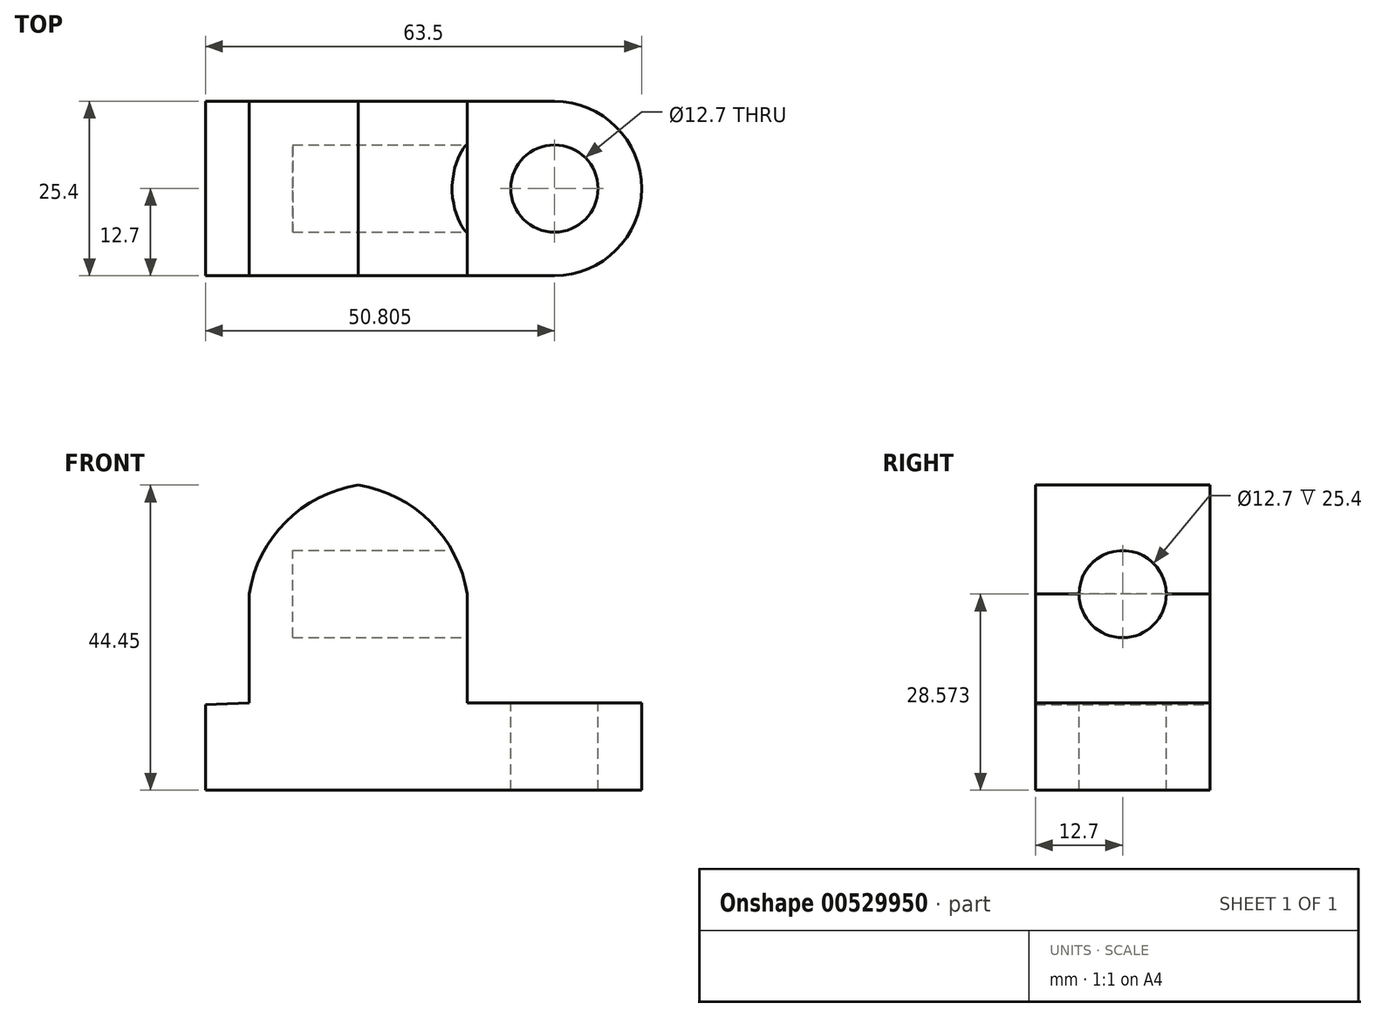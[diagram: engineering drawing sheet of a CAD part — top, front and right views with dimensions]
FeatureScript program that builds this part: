
annotation { "Feature Type Name" : "Feature", "Feature Type Description" : "" }
export const myFeature = defineFeature(function(context is Context, id is Id, definition is map)
    precondition{}
    {
        {
            var Q0;
            Q0=qCreatedBy(makeId("Front.planeOp"),FACE);
            var sketch = newSketch(context, id + "F0", { "sketchPlane" : qUnion([Q0])});
            skLineSegment(sketch, "E0", {"start": v(-67.73, 16.19) * mm, "end": v(-4.23, 16.19) * mm});
            skLineSegment(sketch, "E1", {"start": v(-4.23, 16.19) * mm, "end": v(-4.23, 28.89) * mm});
            skLineSegment(sketch, "E2", {"start": v(-4.23, 28.89) * mm, "end": v(-29.63, 28.89) * mm});
            skLineSegment(sketch, "E3", {"start": v(-29.63, 28.89) * mm, "end": v(-29.63, 60.64) * mm});
            skLineSegment(sketch, "E4", {"start": v(-29.63, 60.64) * mm, "end": v(-61.38, 60.64) * mm});
            skLineSegment(sketch, "E5", {"start": v(-61.38, 60.64) * mm, "end": v(-61.38, 28.89) * mm});
            skLineSegment(sketch, "E6", {"start": v(-67.73, 16.19) * mm, "end": v(-67.73, 28.64) * mm});
            skLineSegment(sketch, "E7", {"start": v(-67.73, 28.64) * mm, "end": v(-61.38, 28.89) * mm});
            skSolve(sketch);
        }
        {
            var Q0;
            Q0 = qSketchRegion(id + "F0", true);
            var Q1;
            Q1=makeQuery(id+"F0.imprint","IMPRINT",FACE,{"disambiguationData":[TD([[makeQuery(id+"F0.imprint","IMPRINT",EDGE,{"derivedFrom":sQuery(id+"F0.wireOp",EDGE,"E0")}),1.0]])]});
            extrude(context, id + "F1", {"entities" : qUnion([Q0, Q1]), "depth" : 25.4 * mm, "offsetDistance" : 25.4 * mm});
        }
        {
            var Q0;
            Q0=makeQuery(id+"F1.opExtrude","SWEPT_FACE",FACE,{"disambiguationData":[OSD([sQuery(id+"F0.wireOp",EDGE,"E2")])]});
            var sketch = newSketch(context, id + "F2", { "sketchPlane" : qUnion([Q0])});
            skArc(sketch, "E8", {"start": v(-16.93, -25.4) * mm, "mid": v(-4.23, -12.7) * mm, "end": v(-16.93, 0) * mm});
            skSolve(sketch);
        }
        {
            var Q0;
            {var subQ0=sQuery(id+"F2.wireOp",EDGE,"E8");var subQ1=sQuery(id+"F0.wireOp",EDGE,"E2");var subQ4=makeQuery(id+"F1.opExtrude","CAP_EDGE",EDGE,{"disambiguationData":[OSD([subQ1])],"isStart":true});var subQ5=makeQuery(id+"F2.imprint","INTERSECT",VERTEX,{"derivedFrom":[subQ4,subQ0]});Q0=makeQuery(id+"F2.imprint","IMPRINT",FACE,{"disambiguationData":[TD([[makeQuery(id+"F2.imprint","IMPRINT",EDGE,{"disambiguationData":[TD([[subQ5,1.0]])],"derivedFrom":subQ0}),-1.0]])]});}
            var Q1;
            {var subQ0=sQuery(id+"F2.wireOp",EDGE,"E8");var subQ1=sQuery(id+"F0.wireOp",EDGE,"E2");var subQ4=makeQuery(id+"F1.opExtrude","CAP_EDGE",EDGE,{"disambiguationData":[OSD([subQ1])],"isStart":false});var subQ5=makeQuery(id+"F2.imprint","INTERSECT",VERTEX,{"derivedFrom":[subQ4,subQ0]});Q1=makeQuery(id+"F2.imprint","IMPRINT",FACE,{"disambiguationData":[TD([[makeQuery(id+"F2.imprint","IMPRINT",EDGE,{"disambiguationData":[TD([[subQ5,-1.0]])],"derivedFrom":subQ0}),-1.0]])]});}
            extrude(context, id + "F3", {"entities" : qUnion([Q0, Q1]), "operationType" : NewBodyOperationType.REMOVE, "oppositeDirection" : true, "depth" : 25.4 * mm, "offsetDistance" : 25.4 * mm});
        }
        {
            var Q0;
            Q0=makeQuery(id+"F1.opExtrude","SWEPT_FACE",FACE,{"disambiguationData":[OSD([sQuery(id+"F0.wireOp",EDGE,"E2")])]});
            var sketch = newSketch(context, id + "F4", { "sketchPlane" : qUnion([Q0])});
            skCircle(sketch, "E9", {"center": v(-16.93, -12.7) * mm, "radius": 6.35 * mm});
            skSolve(sketch);
        }
        {
            var Q0;
            Q0=makeQuery(id+"F4.imprint","IMPRINT",FACE,{"disambiguationData":[TD([[makeQuery(id+"F4.imprint","IMPRINT",EDGE,{"derivedFrom":sQuery(id+"F4.wireOp",EDGE,"E9")}),1.0]])]});
            extrude(context, id + "F5", {"entities" : qUnion([Q0]), "operationType" : NewBodyOperationType.REMOVE, "oppositeDirection" : true, "depth" : 25.4 * mm, "offsetDistance" : 25.4 * mm});
        }
        {
            var Q0;
            Q0=makeQuery(id+"F1.opExtrude","CAP_FACE",FACE,{"disambiguationData":[OSD([sQuery(id+"F0.wireOp",EDGE,"E0"),sQuery(id+"F0.wireOp",EDGE,"E1"),sQuery(id+"F0.wireOp",EDGE,"E2"),sQuery(id+"F0.wireOp",EDGE,"E3"),sQuery(id+"F0.wireOp",EDGE,"E4"),sQuery(id+"F0.wireOp",EDGE,"E5"),sQuery(id+"F0.wireOp",EDGE,"E6"),sQuery(id+"F0.wireOp",EDGE,"E7")])],"isStart":false});
            var sketch = newSketch(context, id + "F6", { "sketchPlane" : qUnion([Q0])});
            skArc(sketch, "E10", {"start": v(-29.63, 44.76) * mm, "mid": v(-34.98, 55.29) * mm, "end": v(-45.5, 60.64) * mm});
            skArc(sketch, "E11", {"start": v(-45.5, 60.64) * mm, "mid": v(-56.02, 55.29) * mm, "end": v(-61.38, 44.76) * mm});
            skSolve(sketch);
        }
        {
            var Q0;
            {var subQ0=sQuery(id+"F6.wireOp",EDGE,"E10");Q0=makeQuery(id+"F6.imprint","IMPRINT",FACE,{"disambiguationData":[TD([[makeQuery(id+"F6.imprint","IMPRINT",EDGE,{"derivedFrom":subQ0}),-1.0]])]});}
            var Q1;
            {var subQ0=sQuery(id+"F6.wireOp",EDGE,"E11");Q1=makeQuery(id+"F6.imprint","IMPRINT",FACE,{"disambiguationData":[TD([[makeQuery(id+"F6.imprint","IMPRINT",EDGE,{"derivedFrom":subQ0}),-1.0]])]});}
            extrude(context, id + "F7", {"entities" : qUnion([Q0, Q1]), "operationType" : NewBodyOperationType.REMOVE, "oppositeDirection" : true, "depth" : 25.4 * mm, "offsetDistance" : 25.4 * mm});
        }
        {
            var Q0;
            Q0=makeQuery(id+"F1.opExtrude","SWEPT_FACE",FACE,{"disambiguationData":[OSD([sQuery(id+"F0.wireOp",EDGE,"E3")])]});
            var sketch = newSketch(context, id + "F8", { "sketchPlane" : qUnion([Q0])});
            skCircle(sketch, "E12", {"center": v(-12.7, 44.76) * mm, "radius": 6.35 * mm});
            skSolve(sketch);
        }
        {
            var Q0;
            {var subQ0=sQuery(id+"F8.wireOp",EDGE,"E12");var subQ1=makeQuery(id+"F7.boolean.opBoolean","COPY",EDGE,{"derivedFrom":makeQuery(id+"F7.opExtrude","SWEPT_EDGE",EDGE,{"disambiguationData":[OSD([sQuery(id+"F0.wireOp",EDGE,"E3"),sQuery(id+"F6.wireOp",EDGE,"E10")])]})});var subQ2=makeQuery(id+"F8.imprint","INTERSECT",VERTEX,{"disambiguationData":[OD(0.0)],"derivedFrom":[subQ1,subQ0]});Q0=makeQuery(id+"F8.imprint","IMPRINT",FACE,{"disambiguationData":[TD([[makeQuery(id+"F8.imprint","IMPRINT",EDGE,{"disambiguationData":[TD([[subQ2,1.0]])],"derivedFrom":subQ0}),1.0]])]});}
            var Q1;
            {var subQ0=sQuery(id+"F8.wireOp",EDGE,"E12");var subQ1=makeQuery(id+"F7.boolean.opBoolean","COPY",EDGE,{"derivedFrom":makeQuery(id+"F7.opExtrude","SWEPT_EDGE",EDGE,{"disambiguationData":[OSD([sQuery(id+"F0.wireOp",EDGE,"E3"),sQuery(id+"F6.wireOp",EDGE,"E10")])]})});var subQ2=makeQuery(id+"F8.imprint","INTERSECT",VERTEX,{"disambiguationData":[OD(0.0)],"derivedFrom":[subQ1,subQ0]});Q1=makeQuery(id+"F8.imprint","IMPRINT",FACE,{"disambiguationData":[TD([[makeQuery(id+"F8.imprint","IMPRINT",EDGE,{"disambiguationData":[TD([[subQ2,-1.0]])],"derivedFrom":subQ0}),1.0]])]});}
            extrude(context, id + "F9", {"entities" : qUnion([Q0, Q1]), "operationType" : NewBodyOperationType.REMOVE, "oppositeDirection" : true, "depth" : 25.4 * mm, "offsetDistance" : 25.4 * mm});
        }
    });
